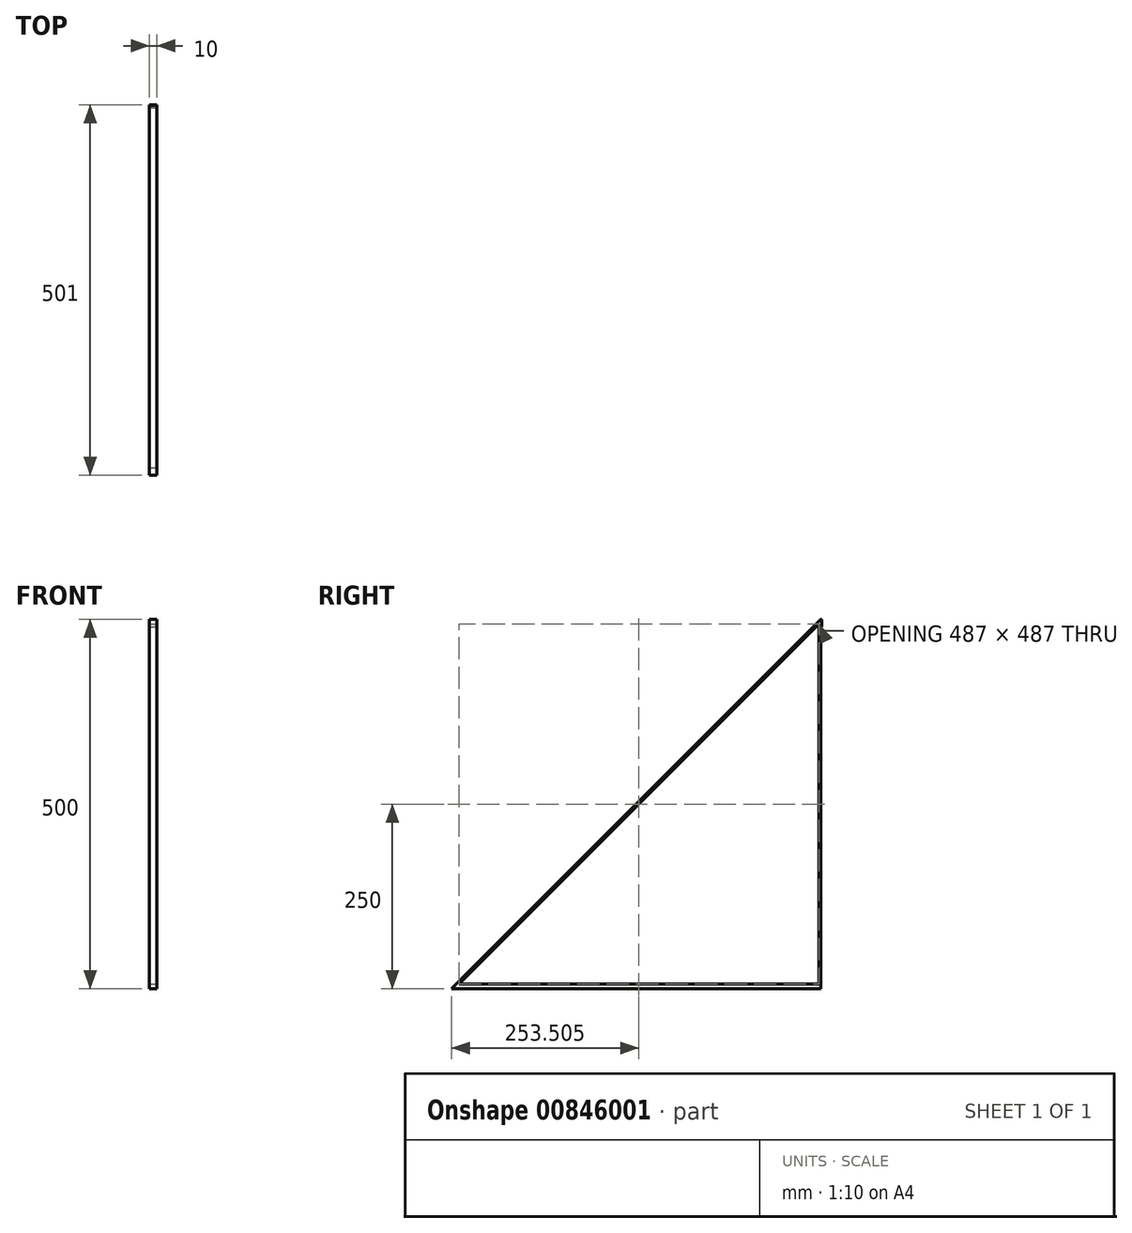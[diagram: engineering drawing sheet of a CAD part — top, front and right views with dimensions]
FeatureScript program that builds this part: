
annotation { "Feature Type Name" : "Feature", "Feature Type Description" : "" }
export const myFeature = defineFeature(function(context is Context, id is Id, definition is map)
    precondition{}
    {
        {
            var Q0;
            Q0=qCreatedBy(makeId("Top.planeOp"),FACE);
            var sketch = newSketch(context, id + "F0", { "sketchPlane" : qUnion([Q0])});
            skLineSegment(sketch, "E0", {"start": v(-17.1, 464.33) * mm, "end": v(-7.1, 464.33) * mm});
            skLineSegment(sketch, "E1", {"start": v(-7.1, 464.33) * mm, "end": v(-7.1, -35.67) * mm});
            skLineSegment(sketch, "E2", {"start": v(-7.1, -35.67) * mm, "end": v(-17.1, -35.67) * mm});
            skLineSegment(sketch, "E3", {"start": v(-17.1, -35.67) * mm, "end": v(-17.1, 464.33) * mm});
            skSolve(sketch);
        }
        {
            var Q0;
            Q0=qSketchRegion(id+"F0",true);
            extrude(context, id + "F1", {"entities" : qUnion([Q0]), "depth" : 500 * mm, "offsetDistance" : 25 * mm});
        }
        {
            var Q0;
            Q0=makeQuery(id+"F1.opExtrude","SWEPT_FACE",FACE,{"disambiguationData":[OSD([sQuery(id+"F0.wireOp",EDGE,"E3")])]});
            var sketch = newSketch(context, id + "F2", { "sketchPlane" : qUnion([Q0])});
            skLineSegment(sketch, "E4", {"start": v(-464.33, 500) * mm, "end": v(35.67, 0) * mm});
            skSolve(sketch);
        }
        {
            var Q0;
            Q0=makeQuery(id+"F2.imprint","IMPRINT",FACE,{"disambiguationData":[TD([[makeQuery(id+"F2.imprint","IMPRINT",EDGE,{"derivedFrom":sQuery(id+"F2.wireOp",EDGE,"E4")}),1.0]])]});
            extrude(context, id + "F3", {"entities" : qUnion([Q0]), "operationType" : NewBodyOperationType.REMOVE, "oppositeDirection" : true, "depth" : 10 * mm, "offsetDistance" : 25 * mm});
        }
        {
            var Q0;
            Q0=makeQuery(id+"F1.opExtrude","SWEPT_FACE",FACE,{"disambiguationData":[OSD([sQuery(id+"F0.wireOp",EDGE,"E1")])]});
            var sketch = newSketch(context, id + "F4", { "sketchPlane" : qUnion([Q0])});
            skPoint(sketch, "E5", {"position": v(461.33, 6.5) * mm});
            skPoint(sketch, "E6", {"position": v(-25.67, 6.5) * mm});
            skPoint(sketch, "E7", {"position": v(461.33, 493.5) * mm});
            skLineSegment(sketch, "E8", {"start": v(-25.67, 6.5) * mm, "end": v(461.33, 6.5) * mm});
            skLineSegment(sketch, "E9", {"start": v(461.33, 6.5) * mm, "end": v(461.33, 493.5) * mm});
            skLineSegment(sketch, "E10", {"start": v(-25.67, 6.5) * mm, "end": v(461.33, 493.5) * mm});
            skSolve(sketch);
        }
        {
            var Q0;
            Q0=makeQuery(id+"F4.imprint","IMPRINT",FACE,{"disambiguationData":[TD([[makeQuery(id+"F4.imprint","IMPRINT",EDGE,{"derivedFrom":sQuery(id+"F4.wireOp",EDGE,"E8")}),1.0]])]});
            extrude(context, id + "F5", {"entities" : qUnion([Q0]), "operationType" : NewBodyOperationType.REMOVE, "oppositeDirection" : true, "depth" : 10 * mm, "offsetDistance" : 25 * mm});
        }
        {
            var Q0;
            Q0=makeQuery(id+"F1.opExtrude","SWEPT_FACE",FACE,{"disambiguationData":[OSD([sQuery(id+"F0.wireOp",EDGE,"E0")])]});
            var sketch = newSketch(context, id + "F6", { "sketchPlane" : qUnion([Q0])});
            skLineSegment(sketch, "E11.bottom", {"start": v(17.1, 500) * mm, "end": v(7.1, 500) * mm});
            skLineSegment(sketch, "E11.top", {"start": v(17.1, 490) * mm, "end": v(7.1, 490) * mm});
            skLineSegment(sketch, "E11.left", {"start": v(17.1, 500) * mm, "end": v(17.1, 490) * mm});
            skLineSegment(sketch, "E11.right", {"start": v(7.1, 500) * mm, "end": v(7.1, 490) * mm});
            skPoint(sketch, "E11.middle", {"position": v(12.1, 495) * mm});
            skSolve(sketch);
        }
        {
            var Q0;
            Q0=makeQuery(id+"F6.imprint","IMPRINT",FACE,{"disambiguationData":[TD([[makeQuery(id+"F6.imprint","IMPRINT",EDGE,{"derivedFrom":sQuery(id+"F6.wireOp",EDGE,"E11.bottom")}),1.0]])]});
            extrude(context, id + "F7", {"entities" : qUnion([Q0]), "operationType" : NewBodyOperationType.ADD, "depth" : 1 * mm, "offsetDistance" : 25 * mm});
        }
    });
